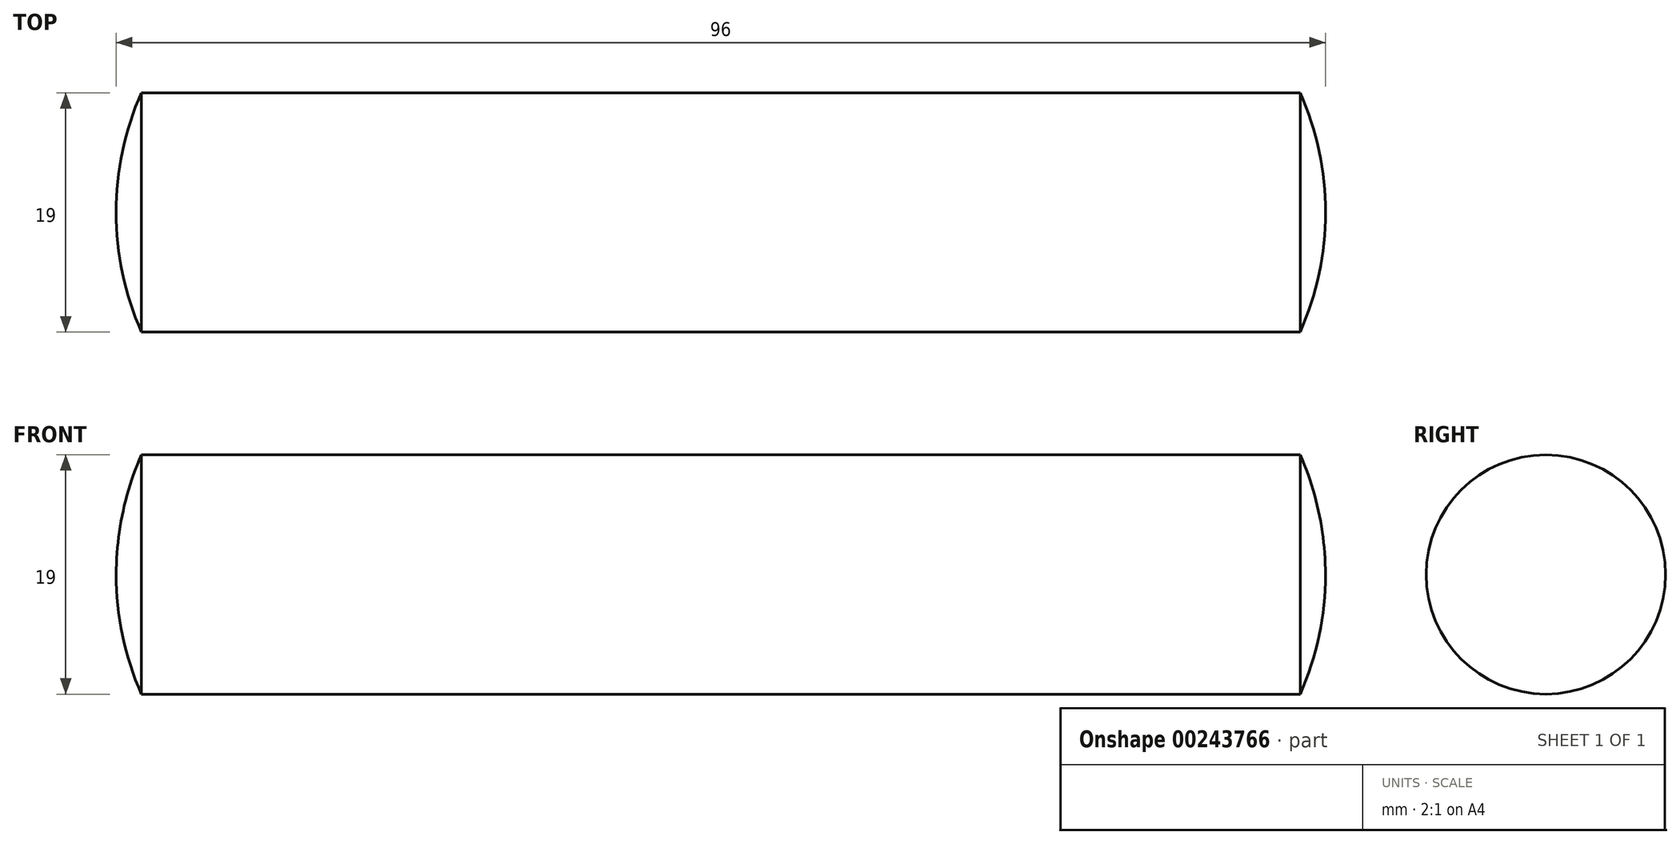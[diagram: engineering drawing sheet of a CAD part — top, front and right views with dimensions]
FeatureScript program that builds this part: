
annotation { "Feature Type Name" : "Feature", "Feature Type Description" : "" }
export const myFeature = defineFeature(function(context is Context, id is Id, definition is map)
    precondition{}
    {
        {
            var Q0;
            Q0=qCreatedBy(makeId("Front.planeOp"),FACE);
            var sketch = newSketch(context, id + "F0", { "sketchPlane" : qUnion([Q0])});
            skLineSegment(sketch, "E0", {"start": v(96, 18.05) * mm, "end": v(96, -21.76) * mm, "construction": true});
            skLineSegment(sketch, "E1", {"start": v(2, 18.05) * mm, "end": v(2, -21.76) * mm, "construction": true});
            skLineSegment(sketch, "E2.0", {"start": v(94, 18.05) * mm, "end": v(94, -21.76) * mm, "construction": true});
            skLineSegment(sketch, "E3", {"start": v(2, 9.5) * mm, "end": v(94, 9.5) * mm});
            skLineSegment(sketch, "E4.MirrorCS", {"start": v(2, -9.5) * mm, "end": v(94, -9.5) * mm, "construction": true});
            skArc(sketch, "E5", {"start": v(2, 9.5) * mm, "mid": v(0.5, 4.85) * mm, "end": v(0, 0) * mm});
            skPoint(sketch, "E6", {"position": v(96, 0) * mm});
            skArc(sketch, "E7", {"start": v(94, -9.5) * mm, "mid": v(95.5, -4.85) * mm, "end": v(96, 0) * mm});
            skArc(sketch, "E8", {"start": v(96, 0) * mm, "mid": v(95.5, 4.85) * mm, "end": v(94, 9.5) * mm});
            skLineSegment(sketch, "E9", {"start": v(0, 0) * mm, "end": v(96, 0) * mm});
            skArc(sketch, "E10", {"start": v(0, 0) * mm, "mid": v(0.5, -4.85) * mm, "end": v(2, -9.5) * mm, "construction": true});
            skLineSegment(sketch, "E11", {"start": v(-7.34, 0) * mm, "end": v(102.97, 0) * mm, "construction": true});
            skSolve(sketch);
        }
        {
            var Q0;
            Q0=makeQuery(id+"F0.imprint","IMPRINT",FACE,{"disambiguationData":[TD([[makeQuery(id+"F0.imprint","IMPRINT",EDGE,{"derivedFrom":sQuery(id+"F0.wireOp",EDGE,"E3")}),-1.0]])]});
            var Q1;
            Q1=sQuery(id+"F0.wireOp",EDGE,"E11");
            revolve(context, id + "F1", {"entities" : qUnion([Q0]), "axis" : qUnion([Q1]), "revolveType" : RevolveType.FULL});
        }
    });
